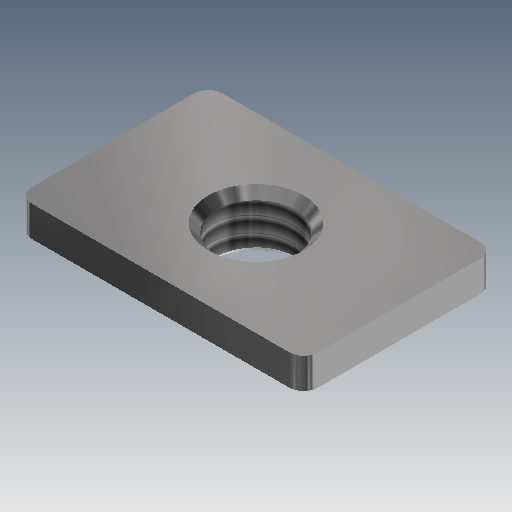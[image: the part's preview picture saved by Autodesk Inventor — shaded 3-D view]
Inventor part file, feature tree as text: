
AUTODESK INVENTOR PART (.ipt)
format: ipt  version: 2017 (Build 210142000, 142)  size: 149,504 bytes
history: native  units: mm
features: other x7, sketch x3, revolve x2, extrude x1, thread x1
ambient origin geometry x8: Origin, YZ Plane, XZ Plane, XY Plane, X Axis, Y Axis, Z Axis, Center Point
bodies: Solid1 (feature_tree)
feature tree (14):
  extrude  "Extrusion1"  TaperAngle=360.0deg  [1 undecoded]
  revolve  "Revolution1"  [1 undecoded]
  revolve  "Revolution2"  [1 undecoded]
  thread  "Thread1"  [1 undecoded]
  other  "dummy_XY"
  other  "dummy_YZ"
  other  "dummy_ZX"
  other  "dummy_X"
  other  "dummy_Y"
  other  "dummy_Z"
  other  "dummy_Center"
  sketch  "Sketch_1"  dims[d0=3.0mm d1=0.0mm d2=360.0deg]
  sketch  "Sketch_2"  dims[d3=360.0deg d4=2.134mm d5=0.0mm]
  sketch  "Sketch_3"
note: 4 required parameter values undecoded (feature->parameter linkage not recoverable at this tier; creation-order binding heuristic only, values carry confidence <= 0.55)